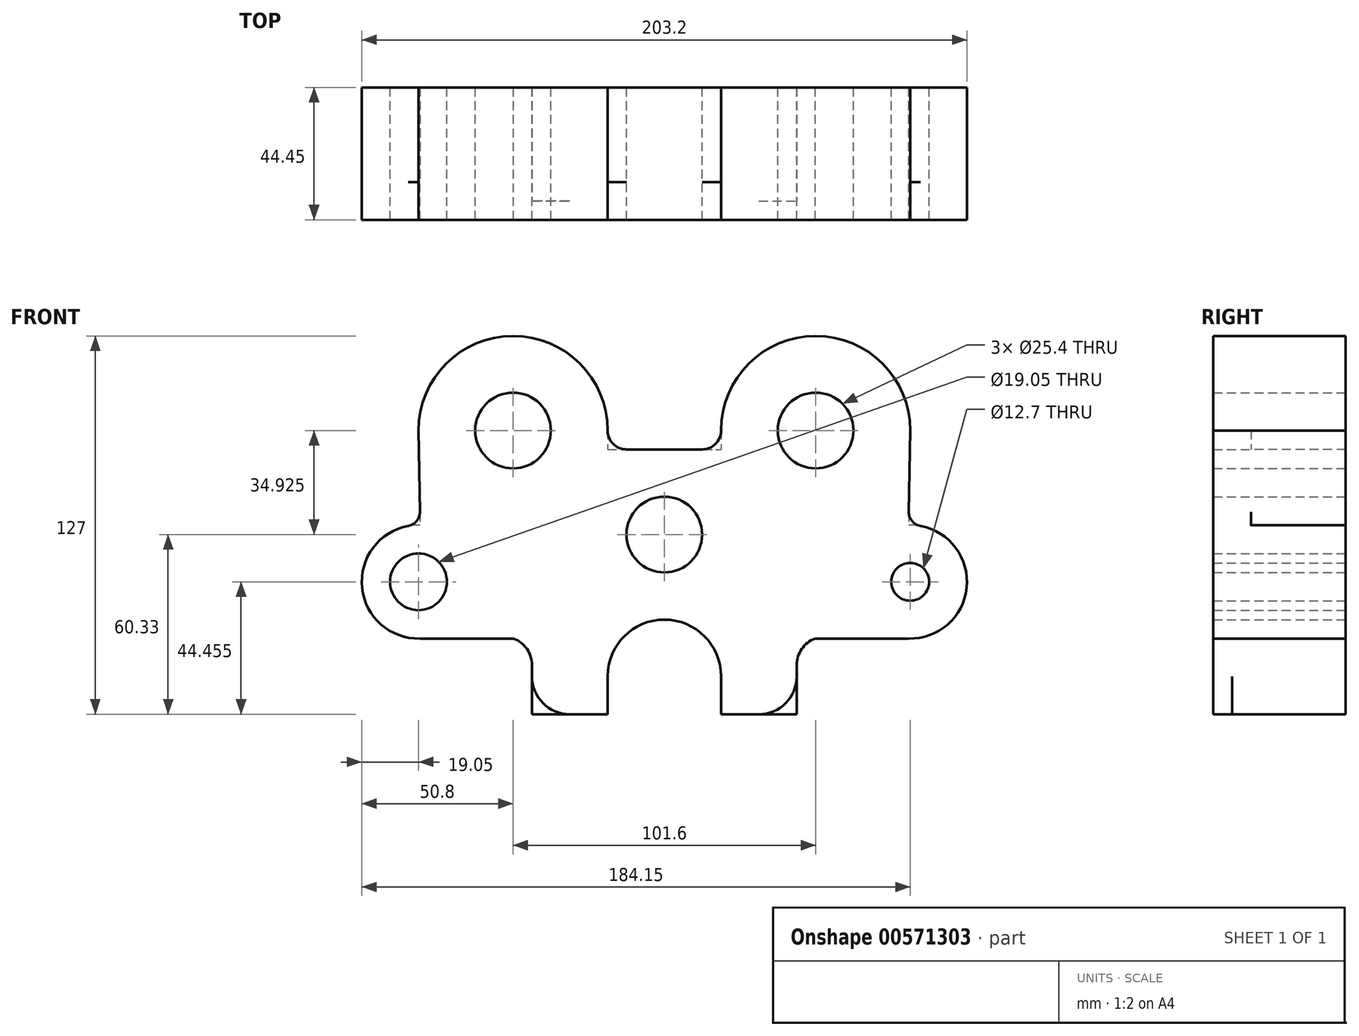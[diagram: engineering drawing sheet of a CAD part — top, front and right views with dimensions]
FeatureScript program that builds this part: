
annotation { "Feature Type Name" : "Feature", "Feature Type Description" : "" }
export const myFeature = defineFeature(function(context is Context, id is Id, definition is map)
    precondition{}
    {
        {
            var Q0;
            Q0=qCreatedBy(makeId("Front.planeOp"),FACE);
            var sketch = newSketch(context, id + "F0", { "sketchPlane" : qUnion([Q0])});
            skCircle(sketch, "E0", {"center": v(0, 0) * mm, "radius": 12.7 * mm});
            skCircle(sketch, "E1", {"center": v(50.8, 34.93) * mm, "radius": 12.7 * mm});
            skCircle(sketch, "E2", {"center": v(82.55, -15.87) * mm, "radius": 9.53 * mm});
            skLineSegment(sketch, "E3", {"start": v(0, 75.85) * mm, "end": v(0, -79.75) * mm, "construction": true});
            skCircle(sketch, "E4.MirrorC", {"center": v(-82.55, -15.87) * mm, "radius": 9.53 * mm});
            skArc(sketch, "E5", {"start": v(-19.05, -47.63) * mm, "mid": v(0, -28.58) * mm, "end": v(19.05, -47.63) * mm});
            skLineSegment(sketch, "E6", {"start": v(-19.05, -47.63) * mm, "end": v(0, -47.63) * mm, "construction": true});
            skLineSegment(sketch, "E7.MirrorCS", {"start": v(19.05, -47.63) * mm, "end": v(0, -47.63) * mm, "construction": true});
            skCircle(sketch, "E8.MirrorC", {"center": v(-50.8, 34.92) * mm, "radius": 12.7 * mm});
            skLineSegment(sketch, "E9", {"start": v(-19.05, -47.63) * mm, "end": v(-19.05, -60.33) * mm});
            skLineSegment(sketch, "E10", {"start": v(-19.05, -60.33) * mm, "end": v(-44.45, -60.33) * mm});
            skLineSegment(sketch, "E11", {"start": v(-44.45, -60.33) * mm, "end": v(-44.45, -43.85) * mm});
            skArc(sketch, "E12", {"start": v(-44.45, -43.85) * mm, "mid": v(-46.15, -38.4) * mm, "end": v(-50.66, -34.92) * mm});
            skLineSegment(sketch, "E13", {"start": v(-50.66, -34.92) * mm, "end": v(-82, -34.92) * mm});
            skArc(sketch, "E14", {"start": v(-82, -34.92) * mm, "mid": v(-101.6, -15.87) * mm, "end": v(-82, 3.17) * mm});
            skArc(sketch, "E15", {"start": v(-82.55, 34.93) * mm, "mid": v(-50.8, 66.67) * mm, "end": v(-19.05, 34.92) * mm});
            skArc(sketch, "E16.MirrorCS", {"start": v(82.55, 34.93) * mm, "mid": v(50.8, 66.68) * mm, "end": v(19.05, 34.93) * mm});
            skArc(sketch, "E17.MirrorCS", {"start": v(82, -34.92) * mm, "mid": v(101.6, -15.87) * mm, "end": v(82, 3.17) * mm});
            skLineSegment(sketch, "E18.MirrorCS", {"start": v(50.66, -34.92) * mm, "end": v(82, -34.92) * mm});
            skLineSegment(sketch, "E19.MirrorCS", {"start": v(44.45, -60.33) * mm, "end": v(44.45, -43.85) * mm});
            skArc(sketch, "E20.MirrorCS", {"start": v(44.45, -43.85) * mm, "mid": v(46.15, -38.4) * mm, "end": v(50.66, -34.92) * mm});
            skLineSegment(sketch, "E21.MirrorCS", {"start": v(19.05, -60.33) * mm, "end": v(44.45, -60.33) * mm});
            skLineSegment(sketch, "E22.MirrorCS", {"start": v(19.05, -47.63) * mm, "end": v(19.05, -60.33) * mm});
            skLineSegment(sketch, "E23", {"start": v(-82.55, 34.93) * mm, "end": v(-82, 3.17) * mm});
            skLineSegment(sketch, "E24", {"start": v(82.55, 34.93) * mm, "end": v(82, 3.17) * mm});
            skLineSegment(sketch, "E25", {"start": v(-19.05, 34.92) * mm, "end": v(-19.05, 28.57) * mm});
            skLineSegment(sketch, "E26.MirrorCS", {"start": v(19.05, 34.92) * mm, "end": v(19.05, 28.57) * mm});
            skLineSegment(sketch, "E27", {"start": v(-19.05, 28.57) * mm, "end": v(19.05, 28.57) * mm});
            skCircle(sketch, "E28", {"center": v(-82.55, -15.87) * mm, "radius": 6.35 * mm});
            skCircle(sketch, "E29.MirrorC", {"center": v(82.55, -15.87) * mm, "radius": 6.35 * mm});
            skSolve(sketch);
        }
        {
            var Q0;
            Q0 = qSketchRegion(id + "F0", true);
            var Q1;
            Q1=makeQuery(id+"F0.imprint","IMPRINT",FACE,{"disambiguationData":[TD([[makeQuery(id+"F0.imprint","IMPRINT",EDGE,{"derivedFrom":sQuery(id+"F0.wireOp",EDGE,"E4.MirrorC")}),-1.0]])]});
            var Q2;
            Q2=makeQuery(id+"F0.imprint","IMPRINT",FACE,{"disambiguationData":[TD([[makeQuery(id+"F0.imprint","IMPRINT",EDGE,{"derivedFrom":sQuery(id+"F0.wireOp",EDGE,"E2")}),1.0]])]});
            extrude(context, id + "F1", {"entities" : qUnion([Q0, Q1, Q2]), "endBound" : BoundingType.SYMMETRIC, "depth" : 12.7 * mm, "offsetDistance" : 25.4 * mm});
        }
        {
            var Q0;
            Q0=makeQuery(id+"F1.opExtrude","SWEPT_EDGE",EDGE,{"disambiguationData":[OSD([sQuery(id+"F0.wireOp",EDGE,"E10"),sQuery(id+"F0.wireOp",EDGE,"E11")])]});
            var Q1;
            Q1=makeQuery(id+"F1.opExtrude","SWEPT_EDGE",EDGE,{"disambiguationData":[OSD([sQuery(id+"F0.wireOp",EDGE,"E19.MirrorCS"),sQuery(id+"F0.wireOp",EDGE,"E21.MirrorCS")])]});
            fillet(context, id + "F2", {"entities" : qUnion([Q0, Q1]), "radius" : 12.7 * mm, "tangentPropagation" : true, "allowEdgeOverflow" : false});
        }
        {
            var Q0;
            Q0=makeQuery(id+"F1.opExtrude","SWEPT_EDGE",EDGE,{"disambiguationData":[OSD([sQuery(id+"F0.wireOp",EDGE,"E14"),sQuery(id+"F0.wireOp",EDGE,"E23")])]});
            var Q1;
            Q1=makeQuery(id+"F1.opExtrude","SWEPT_EDGE",EDGE,{"disambiguationData":[OSD([sQuery(id+"F0.wireOp",EDGE,"E17.MirrorCS"),sQuery(id+"F0.wireOp",EDGE,"E24")])]});
            fillet(context, id + "F3", {"entities" : qUnion([Q0, Q1]), "radius" : 4.76 * mm, "tangentPropagation" : true, "allowEdgeOverflow" : false});
        }
        {
            var Q0;
            Q0=makeQuery(id+"F1.opExtrude","SWEPT_EDGE",EDGE,{"disambiguationData":[OSD([sQuery(id+"F0.wireOp",EDGE,"E25"),sQuery(id+"F0.wireOp",EDGE,"E27")])]});
            var Q1;
            Q1=makeQuery(id+"F1.opExtrude","SWEPT_EDGE",EDGE,{"disambiguationData":[OSD([sQuery(id+"F0.wireOp",EDGE,"E26.MirrorCS"),sQuery(id+"F0.wireOp",EDGE,"E27")])]});
            fillet(context, id + "F4", {"entities" : qUnion([Q0, Q1]), "radius" : 6.35 * mm, "tangentPropagation" : true, "allowEdgeOverflow" : false});
        }
        {
            var Q0;
            Q0=makeQuery(id+"F0.imprint","IMPRINT",FACE,{"disambiguationData":[TD([[makeQuery(id+"F0.imprint","IMPRINT",EDGE,{"derivedFrom":sQuery(id+"F0.wireOp",EDGE,"E4.MirrorC")}),-1.0]])]});
            var Q1;
            Q1=makeQuery(id+"F0.imprint","IMPRINT",FACE,{"disambiguationData":[TD([[makeQuery(id+"F0.imprint","IMPRINT",EDGE,{"derivedFrom":sQuery(id+"F0.wireOp",EDGE,"E2")}),1.0]])]});
            extrude(context, id + "F5", {"entities" : qUnion([Q0, Q1]), "operationType" : NewBodyOperationType.ADD, "oppositeDirection" : true, "depth" : 38.1 * mm, "offsetDistance" : 25.4 * mm});
        }
    });
